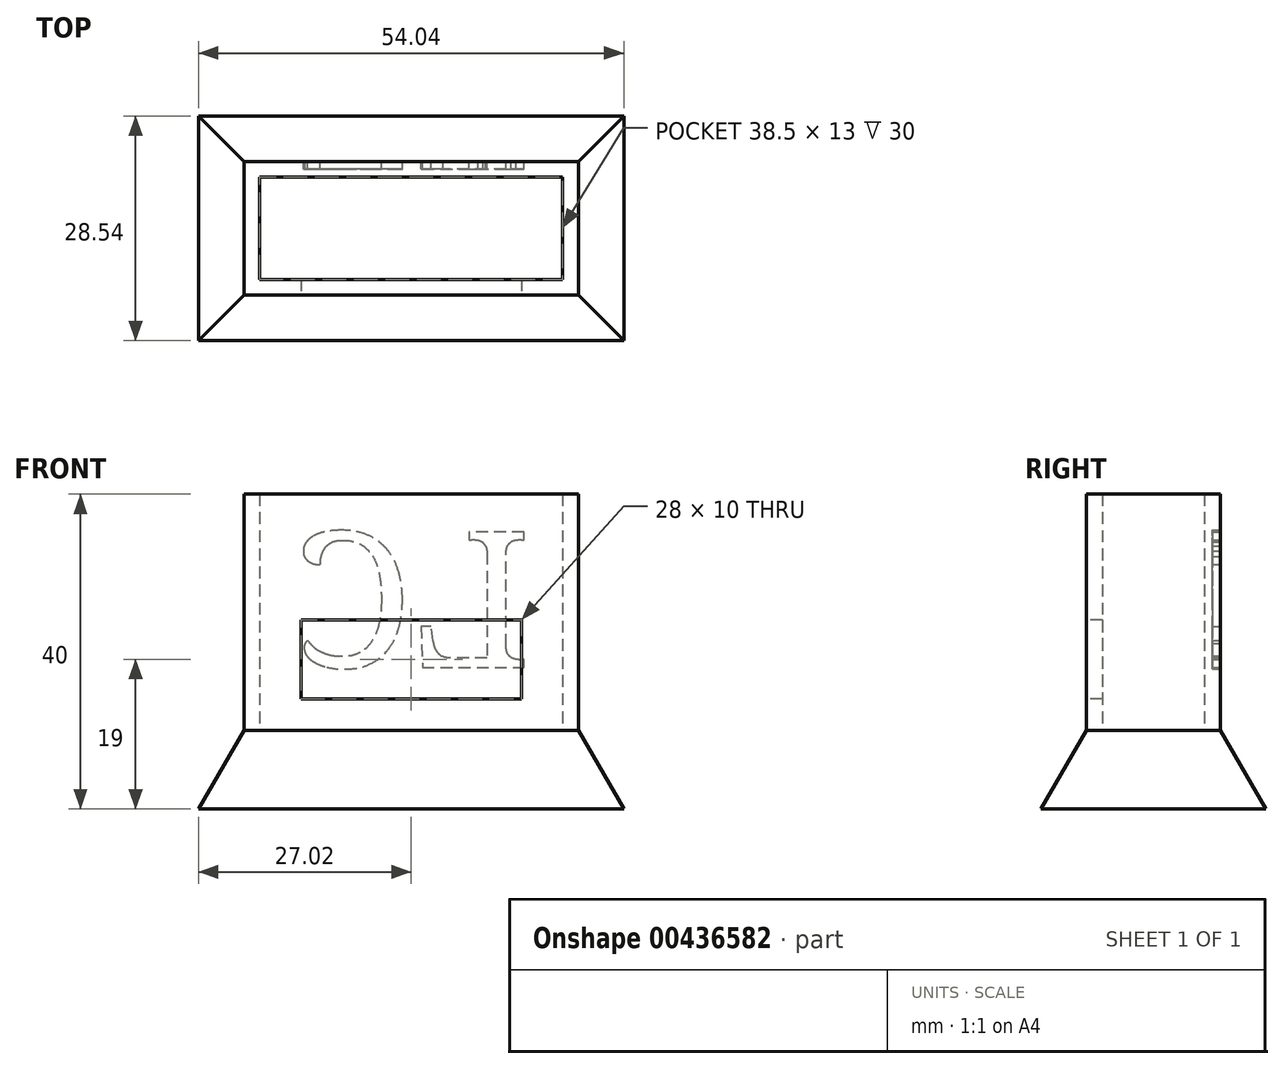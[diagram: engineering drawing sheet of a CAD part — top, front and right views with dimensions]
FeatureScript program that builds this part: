
annotation { "Feature Type Name" : "Feature", "Feature Type Description" : "" }
export const myFeature = defineFeature(function(context is Context, id is Id, definition is map)
    precondition{}
    {
        {
            var Q0;
            Q0=qCreatedBy(makeId("Top.planeOp"),FACE);
            var sketch = newSketch(context, id + "F0", { "sketchPlane" : qUnion([Q0])});
            skLineSegment(sketch, "E0.bottom", {"start": v(21.25, 8.5) * mm, "end": v(-21.25, 8.5) * mm});
            skLineSegment(sketch, "E0.top", {"start": v(21.25, -8.5) * mm, "end": v(-21.25, -8.5) * mm});
            skLineSegment(sketch, "E0.left", {"start": v(21.25, 8.5) * mm, "end": v(21.25, -8.5) * mm});
            skLineSegment(sketch, "E0.right", {"start": v(-21.25, 8.5) * mm, "end": v(-21.25, -8.5) * mm});
            skPoint(sketch, "E0.middle", {"position": v(0, 0) * mm});
            skLineSegment(sketch, "E1.bottom", {"start": v(19.25, 6.5) * mm, "end": v(-19.25, 6.5) * mm});
            skLineSegment(sketch, "E1.top", {"start": v(19.25, -6.5) * mm, "end": v(-19.25, -6.5) * mm});
            skLineSegment(sketch, "E1.left", {"start": v(19.25, 6.5) * mm, "end": v(19.25, -6.5) * mm});
            skLineSegment(sketch, "E1.right", {"start": v(-19.25, 6.5) * mm, "end": v(-19.25, -6.5) * mm});
            skSolve(sketch);
        }
        {
            var Q0;
            Q0 = qSketchRegion(id + "F0", true);
            extrude(context, id + "F1", {"entities" : qUnion([Q0]), "depth" : 30 * mm});
        }
        {
            var Q0;
            Q0=makeQuery(id+"F1.opExtrude","CAP_FACE",FACE,{"disambiguationData":[OSD([sQuery(id+"F0.wireOp",EDGE,"E0.bottom"),sQuery(id+"F0.wireOp",EDGE,"E0.top"),sQuery(id+"F0.wireOp",EDGE,"E0.left"),sQuery(id+"F0.wireOp",EDGE,"E0.right"),sQuery(id+"F0.wireOp",EDGE,"E1.bottom"),sQuery(id+"F0.wireOp",EDGE,"E1.top"),sQuery(id+"F0.wireOp",EDGE,"E1.left"),sQuery(id+"F0.wireOp",EDGE,"E1.right")])],"isStart":true});
            var sketch = newSketch(context, id + "F2", { "sketchPlane" : qUnion([Q0])});
            skLineSegment(sketch, "E2.bottom", {"start": v(21.25, 8.5) * mm, "end": v(-21.25, 8.5) * mm});
            skLineSegment(sketch, "E2.top", {"start": v(21.25, -8.5) * mm, "end": v(-21.25, -8.5) * mm});
            skLineSegment(sketch, "E2.left", {"start": v(21.25, 8.5) * mm, "end": v(21.25, -8.5) * mm});
            skLineSegment(sketch, "E2.right", {"start": v(-21.25, 8.5) * mm, "end": v(-21.25, -8.5) * mm});
            skPoint(sketch, "E2.middle", {"position": v(0, 0) * mm});
            skSolve(sketch);
        }
        {
            var Q0;
            Q0 = qSketchRegion(id + "F2", true);
            extrude(context, id + "F3", {"entities" : qUnion([Q0]), "operationType" : NewBodyOperationType.ADD, "depth" : 10 * mm, "hasDraft" : true, "draftAngle" : 30 * degree});
        }
        {
            var Q0;
            Q0=makeQuery(id+"F1.opExtrude","SWEPT_FACE",FACE,{"disambiguationData":[OSD([sQuery(id+"F0.wireOp",EDGE,"E0.bottom")])]});
            var sketch = newSketch(context, id + "F4", { "sketchPlane" : qUnion([Q0])});
            skLineSegment(sketch, "E3", {"start": v(-21.25, 8) * mm, "end": v(21.25, 8) * mm, "construction": true});
            skLineSegment(sketch, "E4.bottom", {"start": v(-15.25, 8) * mm, "end": v(15.25, 8) * mm, "construction": true});
            skLineSegment(sketch, "E4.top", {"start": v(-15.25, 30) * mm, "end": v(15.25, 30) * mm, "construction": true});
            skLineSegment(sketch, "E4.left", {"start": v(-15.25, 8) * mm, "end": v(-15.25, 30) * mm, "construction": true});
            skLineSegment(sketch, "E4.right", {"start": v(15.25, 8) * mm, "end": v(15.25, 30) * mm, "construction": true});
            skText(sketch, "E5", { "text": "LC", "fontName": "NotoSerif-Regular.ttf"});
            const initialGuessF4  = {"E5": [-0.01525, 0.008, 1, 0, 0.01732]};
            skSetInitialGuess(sketch, initialGuessF4);
            skSolve(sketch);
        }
        {
            var Q0;
            Q0 = qSketchRegion(id + "F4", true);
            extrude(context, id + "F5", {"entities" : qUnion([Q0]), "operationType" : NewBodyOperationType.REMOVE, "oppositeDirection" : true, "depth" : 1 * mm});
        }
        {
            var Q0;
            Q0=makeQuery(id+"F1.opExtrude","SWEPT_FACE",FACE,{"disambiguationData":[OSD([sQuery(id+"F0.wireOp",EDGE,"E0.top")])]});
            var sketch = newSketch(context, id + "F6", { "sketchPlane" : qUnion([Q0])});
            skLineSegment(sketch, "E6.bottom", {"start": v(-14, 4) * mm, "end": v(14, 4) * mm});
            skLineSegment(sketch, "E6.top", {"start": v(-14, 14) * mm, "end": v(14, 14) * mm});
            skLineSegment(sketch, "E6.left", {"start": v(-14, 4) * mm, "end": v(-14, 14) * mm});
            skLineSegment(sketch, "E6.right", {"start": v(14, 4) * mm, "end": v(14, 14) * mm});
            skLineSegment(sketch, "E7", {"start": v(0, 14) * mm, "end": v(0, -34.33) * mm, "construction": true});
            skSolve(sketch);
        }
        {
            var Q0;
            Q0 = qSketchRegion(id + "F6", true);
            extrude(context, id + "F7", {"entities" : qUnion([Q0]), "operationType" : NewBodyOperationType.REMOVE, "endBound" : BoundingType.UP_TO_NEXT, "oppositeDirection" : true, "depth" : 25 * mm});
        }
    });
